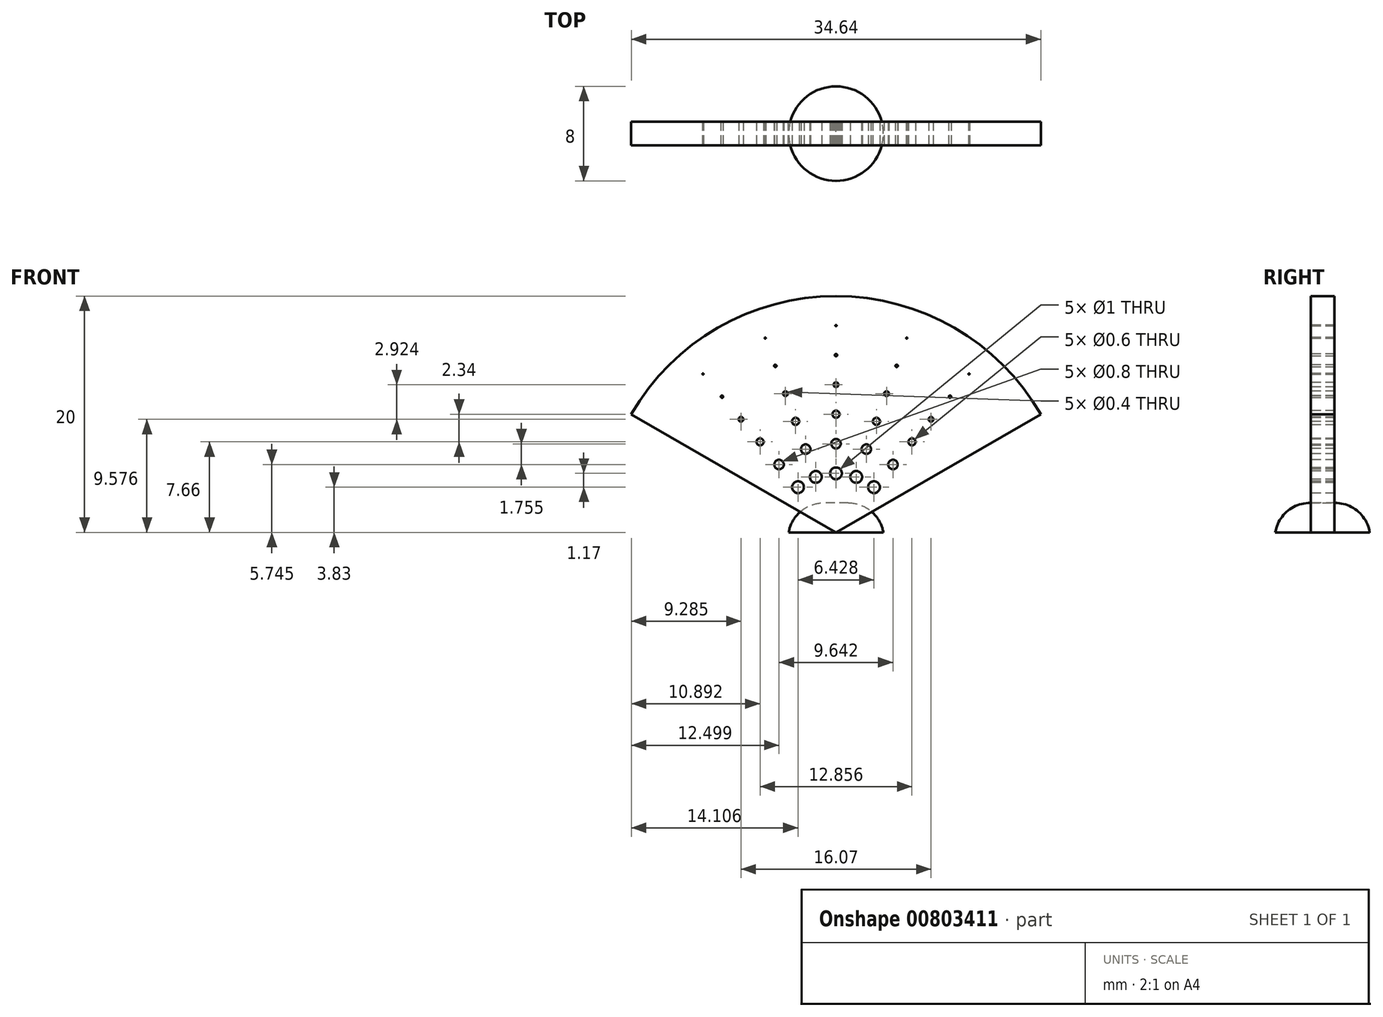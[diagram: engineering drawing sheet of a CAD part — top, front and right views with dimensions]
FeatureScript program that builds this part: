
annotation { "Feature Type Name" : "Feature", "Feature Type Description" : "" }
export const myFeature = defineFeature(function(context is Context, id is Id, definition is map)
    precondition{}
    {
        {
            var Q0;
            Q0=qCreatedBy(makeId("Right.planeOp"),FACE);
            var sketch = newSketch(context, id + "F0", { "sketchPlane" : qUnion([Q0])});
            skLineSegment(sketch, "E0.bottom", {"start": v(0, 0) * mm, "end": v(2, 0) * mm});
            skLineSegment(sketch, "E0.top", {"start": v(0, 20) * mm, "end": v(2, 20) * mm});
            skLineSegment(sketch, "E0.left", {"start": v(0, 0) * mm, "end": v(0, 20) * mm});
            skLineSegment(sketch, "E0.right", {"start": v(2, 0) * mm, "end": v(2, 20) * mm});
            skSolve(sketch);
        }
        {
            var Q0;
            Q0=makeQuery(id+"F0.imprint","IMPRINT",FACE,{"disambiguationData":[TD([[makeQuery(id+"F0.imprint","IMPRINT",EDGE,{"derivedFrom":sQuery(id+"F0.wireOp",EDGE,"E0.bottom")}),1.0]])]});
            var Q1;
            Q1=sQuery(id+"F0.wireOp",EDGE,"E0.bottom");
            revolve(context, id + "F1", {"surfaceOperationType" : NewSurfaceOperationType.NEW, "entities" : qUnion([Q0]), "axis" : qUnion([Q1]), "revolveType" : RevolveType.TWO_DIRECTIONS, "angle" : 60 * degree, "angleBack" : 300 * degree});
        }
        {
            var Q0;
            Q0=qCreatedBy(makeId("Top.planeOp"),FACE);
            var sketch = newSketch(context, id + "F2", { "sketchPlane" : qUnion([Q0])});
            skLineSegment(sketch, "E1", {"start": v(0, 0) * mm, "end": v(0, 1) * mm});
            skCircle(sketch, "E2", {"center": v(0, 1) * mm, "radius": 4 * mm});
            skSolve(sketch);
        }
        {
            var Q0;
            Q0=makeQuery(id+"F2.imprint","IMPRINT",FACE,{"disambiguationData":[TD([[makeQuery(id+"F2.imprint","IMPRINT",EDGE,{"derivedFrom":sQuery(id+"F2.wireOp",EDGE,"E2")}),1.0]])]});
            extrude(context, id + "F3", {"entities" : qUnion([Q0]), "depth" : 2.5 * mm, "offsetDistance" : 25 * mm});
        }
        {
            var Q0;
            Q0=makeQuery(id+"F3.opExtrude","CAP_EDGE",EDGE,{"disambiguationData":[OSD([sQuery(id+"F2.wireOp",EDGE,"E2")])],"isStart":false});
            fillet(context, id + "F4", {"entities" : qUnion([Q0]), "radius" : 3 * mm, "tangentPropagation" : true, "allowEdgeOverflow" : false});
        }
        {
            var Q0;
            Q0=makeQuery(id+"F1.opRevolve","SWEPT_FACE",FACE,{"disambiguationData":[OSD([sQuery(id+"F0.wireOp",EDGE,"E0.left")])]});
            var sketch = newSketch(context, id + "F5", { "sketchPlane" : qUnion([Q0])});
            skCircle(sketch, "E3", {"center": v(0, 5) * mm, "radius": 0.5 * mm});
            skCircle(sketch, "E4", {"center": v(0, 7.5) * mm, "radius": 0.4 * mm});
            skCircle(sketch, "E5", {"center": v(0, 10) * mm, "radius": 0.3 * mm});
            skCircle(sketch, "E6", {"center": v(0, 12.5) * mm, "radius": 0.2 * mm});
            skCircle(sketch, "E7", {"center": v(0, 15) * mm, "radius": 0.1 * mm});
            skCircle(sketch, "E8", {"center": v(0, 17.5) * mm, "radius": 0.05 * mm});
            skCircle(sketch, "E9.1.0", {"center": v(-5.99, 16.44) * mm, "radius": 0.05 * mm});
            skCircle(sketch, "E9.1.1", {"center": v(-5.13, 14.1) * mm, "radius": 0.1 * mm});
            skCircle(sketch, "E9.1.2", {"center": v(-4.28, 11.75) * mm, "radius": 0.2 * mm});
            skCircle(sketch, "E9.1.3", {"center": v(-3.42, 9.4) * mm, "radius": 0.3 * mm});
            skCircle(sketch, "E9.1.4", {"center": v(-2.57, 7.05) * mm, "radius": 0.4 * mm});
            skCircle(sketch, "E9.1.5", {"center": v(-1.71, 4.7) * mm, "radius": 0.5 * mm});
            skCircle(sketch, "E9.2.0", {"center": v(-11.25, 13.4) * mm, "radius": 0.05 * mm});
            skCircle(sketch, "E9.2.1", {"center": v(-9.64, 11.5) * mm, "radius": 0.1 * mm});
            skCircle(sketch, "E9.2.2", {"center": v(-8.03, 9.58) * mm, "radius": 0.2 * mm});
            skCircle(sketch, "E9.2.3", {"center": v(-6.43, 7.66) * mm, "radius": 0.3 * mm});
            skCircle(sketch, "E9.2.4", {"center": v(-4.82, 5.75) * mm, "radius": 0.4 * mm});
            skCircle(sketch, "E9.2.5", {"center": v(-3.21, 3.83) * mm, "radius": 0.5 * mm});
            skCircle(sketch, "E9.16.0", {"center": v(11.25, 13.4) * mm, "radius": 0.05 * mm});
            skCircle(sketch, "E9.16.1", {"center": v(9.64, 11.5) * mm, "radius": 0.1 * mm});
            skCircle(sketch, "E9.16.2", {"center": v(8.03, 9.58) * mm, "radius": 0.2 * mm});
            skCircle(sketch, "E9.16.3", {"center": v(6.43, 7.66) * mm, "radius": 0.3 * mm});
            skCircle(sketch, "E9.16.4", {"center": v(4.82, 5.75) * mm, "radius": 0.4 * mm});
            skCircle(sketch, "E9.16.5", {"center": v(3.21, 3.83) * mm, "radius": 0.5 * mm});
            skCircle(sketch, "E9.17.0", {"center": v(5.99, 16.44) * mm, "radius": 0.05 * mm});
            skCircle(sketch, "E9.17.1", {"center": v(5.13, 14.1) * mm, "radius": 0.1 * mm});
            skCircle(sketch, "E9.17.2", {"center": v(4.28, 11.75) * mm, "radius": 0.2 * mm});
            skCircle(sketch, "E9.17.3", {"center": v(3.42, 9.4) * mm, "radius": 0.3 * mm});
            skCircle(sketch, "E9.17.4", {"center": v(2.57, 7.05) * mm, "radius": 0.4 * mm});
            skCircle(sketch, "E9.17.5", {"center": v(1.71, 4.7) * mm, "radius": 0.5 * mm});
            skSolve(sketch);
        }
        {
            var Q0;
            Q0 = qSketchRegion(id + "F5", true);
            extrude(context, id + "F6", {"entities" : qUnion([Q0]), "operationType" : NewBodyOperationType.REMOVE, "oppositeDirection" : true, "depth" : 25 * mm, "offsetDistance" : 25 * mm});
        }
    });
